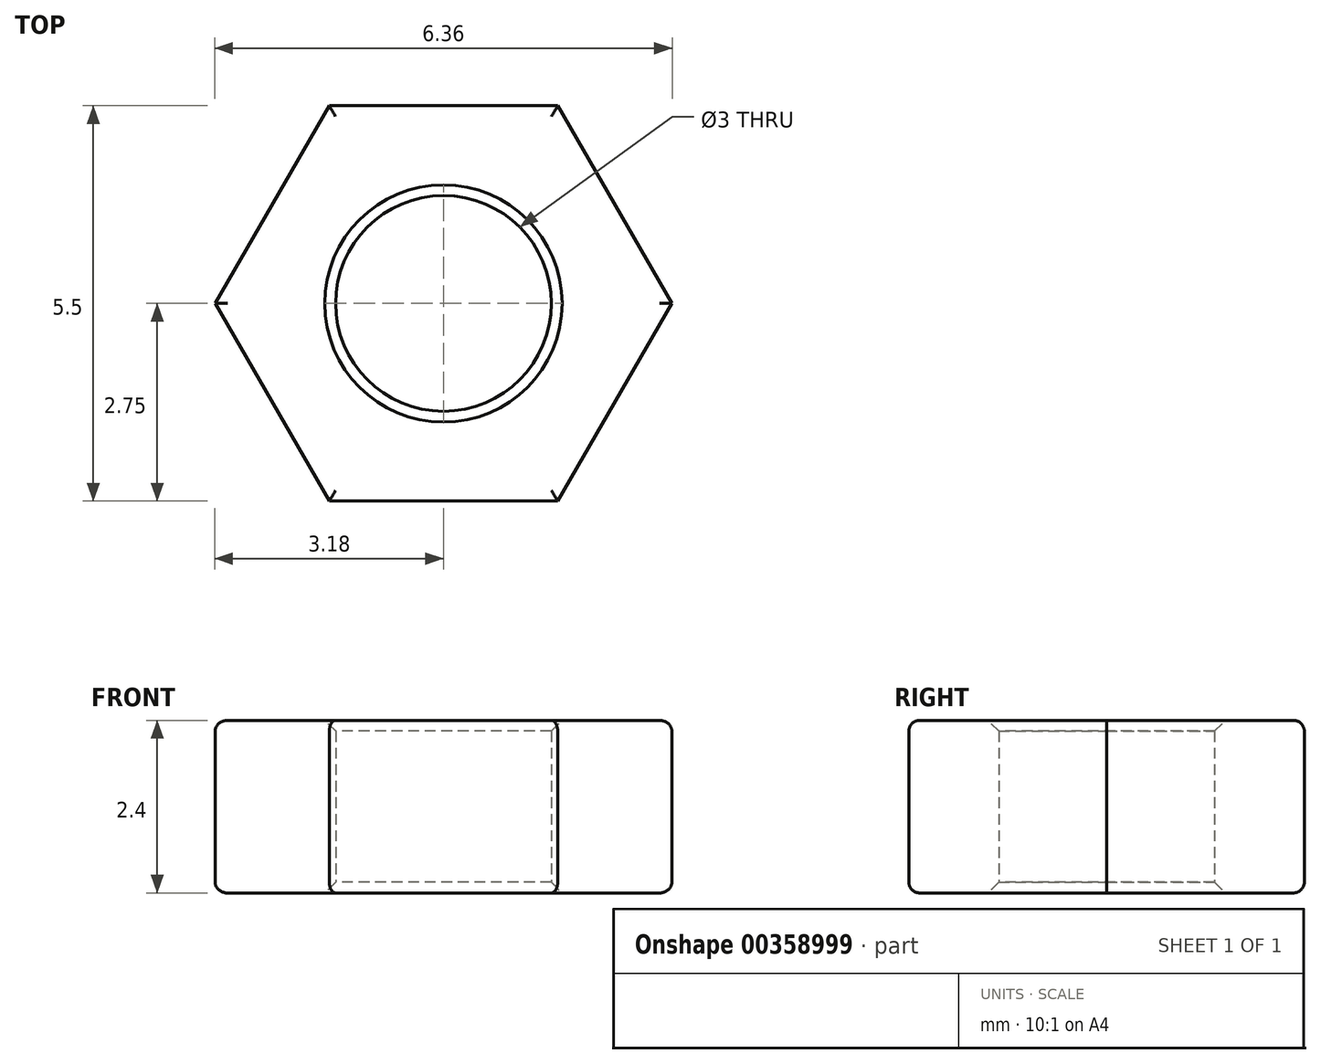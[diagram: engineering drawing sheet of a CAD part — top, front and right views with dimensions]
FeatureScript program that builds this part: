
annotation { "Feature Type Name" : "Feature", "Feature Type Description" : "" }
export const myFeature = defineFeature(function(context is Context, id is Id, definition is map)
    precondition{}
    {
        {
            assignVariable(context, id + "F0", {"name" : "d", "anyValue" : 3});
        }
        {
            assignVariable(context, id + "F1", {"name" : "L", "anyValue" : 2.4});
        }
        {
            var Q0;
            Q0=qCreatedBy(makeId("Top.planeOp"),FACE);
            var sketch = newSketch(context, id + "F2", { "sketchPlane" : qUnion([Q0])});
            skCircle(sketch, "E0", {"center": v(0, 0) * mm, "radius": 1.5 * mm});
            skCircle(sketch, "E1.cCircle", {"center": v(0, 0) * mm, "radius": 2.75 * mm, "construction": true});
            skLineSegment(sketch, "E1.0", {"start": v(-1.59, 2.75) * mm, "end": v(1.59, 2.75) * mm});
            skLineSegment(sketch, "E1.1", {"start": v(1.59, 2.75) * mm, "end": v(3.18, 0) * mm});
            skLineSegment(sketch, "E1.2", {"start": v(3.18, 0) * mm, "end": v(1.59, -2.75) * mm});
            skLineSegment(sketch, "E1.3", {"start": v(1.59, -2.75) * mm, "end": v(-1.59, -2.75) * mm});
            skLineSegment(sketch, "E1.4", {"start": v(-1.59, -2.75) * mm, "end": v(-3.18, 0) * mm});
            skLineSegment(sketch, "E1.5", {"start": v(-3.18, 0) * mm, "end": v(-1.59, 2.75) * mm});
            skPoint(sketch, "E1.0.midPoint", {"position": v(0, 2.75) * mm});
            skSolve(sketch);
        }
        {
            var Q0;
            Q0 = qSketchRegion(id + "F2", true);
            extrude(context, id + "F3", {"entities" : qUnion([Q0]), "depth" : (getVariable(context, 'L')) * mm});
        }
        {
            var Q0;
            Q0=makeQuery(id+"F3.opExtrude","CAP_EDGE",EDGE,{"disambiguationData":[OSD([sQuery(id+"F2.wireOp",EDGE,"E1.2")])],"isStart":false});
            var Q1;
            Q1=makeQuery(id+"F3.opExtrude","CAP_EDGE",EDGE,{"disambiguationData":[OSD([sQuery(id+"F2.wireOp",EDGE,"E1.1")])],"isStart":false});
            var Q2;
            Q2=makeQuery(id+"F3.opExtrude","CAP_EDGE",EDGE,{"disambiguationData":[OSD([sQuery(id+"F2.wireOp",EDGE,"E1.0")])],"isStart":false});
            var Q3;
            Q3=makeQuery(id+"F3.opExtrude","CAP_EDGE",EDGE,{"disambiguationData":[OSD([sQuery(id+"F2.wireOp",EDGE,"E1.5")])],"isStart":false});
            var Q4;
            Q4=makeQuery(id+"F3.opExtrude","CAP_EDGE",EDGE,{"disambiguationData":[OSD([sQuery(id+"F2.wireOp",EDGE,"E1.4")])],"isStart":false});
            var Q5;
            Q5=makeQuery(id+"F3.opExtrude","CAP_EDGE",EDGE,{"disambiguationData":[OSD([sQuery(id+"F2.wireOp",EDGE,"E1.3")])],"isStart":false});
            var Q6;
            Q6=makeQuery(id+"F3.opExtrude","CAP_EDGE",EDGE,{"disambiguationData":[OSD([sQuery(id+"F2.wireOp",EDGE,"E1.3")])],"isStart":true});
            var Q7;
            Q7=makeQuery(id+"F3.opExtrude","CAP_EDGE",EDGE,{"disambiguationData":[OSD([sQuery(id+"F2.wireOp",EDGE,"E1.2")])],"isStart":true});
            var Q8;
            Q8=makeQuery(id+"F3.opExtrude","CAP_EDGE",EDGE,{"disambiguationData":[OSD([sQuery(id+"F2.wireOp",EDGE,"E1.4")])],"isStart":true});
            var Q9;
            Q9=makeQuery(id+"F3.opExtrude","CAP_EDGE",EDGE,{"disambiguationData":[OSD([sQuery(id+"F2.wireOp",EDGE,"E1.5")])],"isStart":true});
            var Q10;
            Q10=makeQuery(id+"F3.opExtrude","CAP_EDGE",EDGE,{"disambiguationData":[OSD([sQuery(id+"F2.wireOp",EDGE,"E1.0")])],"isStart":true});
            var Q11;
            Q11=makeQuery(id+"F3.opExtrude","CAP_EDGE",EDGE,{"disambiguationData":[OSD([sQuery(id+"F2.wireOp",EDGE,"E1.1")])],"isStart":true});
            fillet(context, id + "F4", {"entities" : qUnion([Q0, Q1, Q2, Q3, Q4, Q5, Q6, Q7, Q8, Q9, Q10, Q11]), "radius" : (getVariable(context, 'd') / 20) * mm, "tangentPropagation" : true, "allowEdgeOverflow" : false});
        }
        {
            var Q0;
            Q0=makeQuery(id+"F3.opExtrude","CAP_EDGE",EDGE,{"disambiguationData":[OSD([sQuery(id+"F2.wireOp",EDGE,"E0")])],"isStart":false});
            var Q1;
            Q1=makeQuery(id+"F3.opExtrude","CAP_EDGE",EDGE,{"disambiguationData":[OSD([sQuery(id+"F2.wireOp",EDGE,"E0")])],"isStart":true});
            chamfer(context, id + "F5", {"entities" : qUnion([Q0, Q1]), "width" : (getVariable(context, 'd') / 20) * mm, "tangentPropagation" : true});
        }
    });
